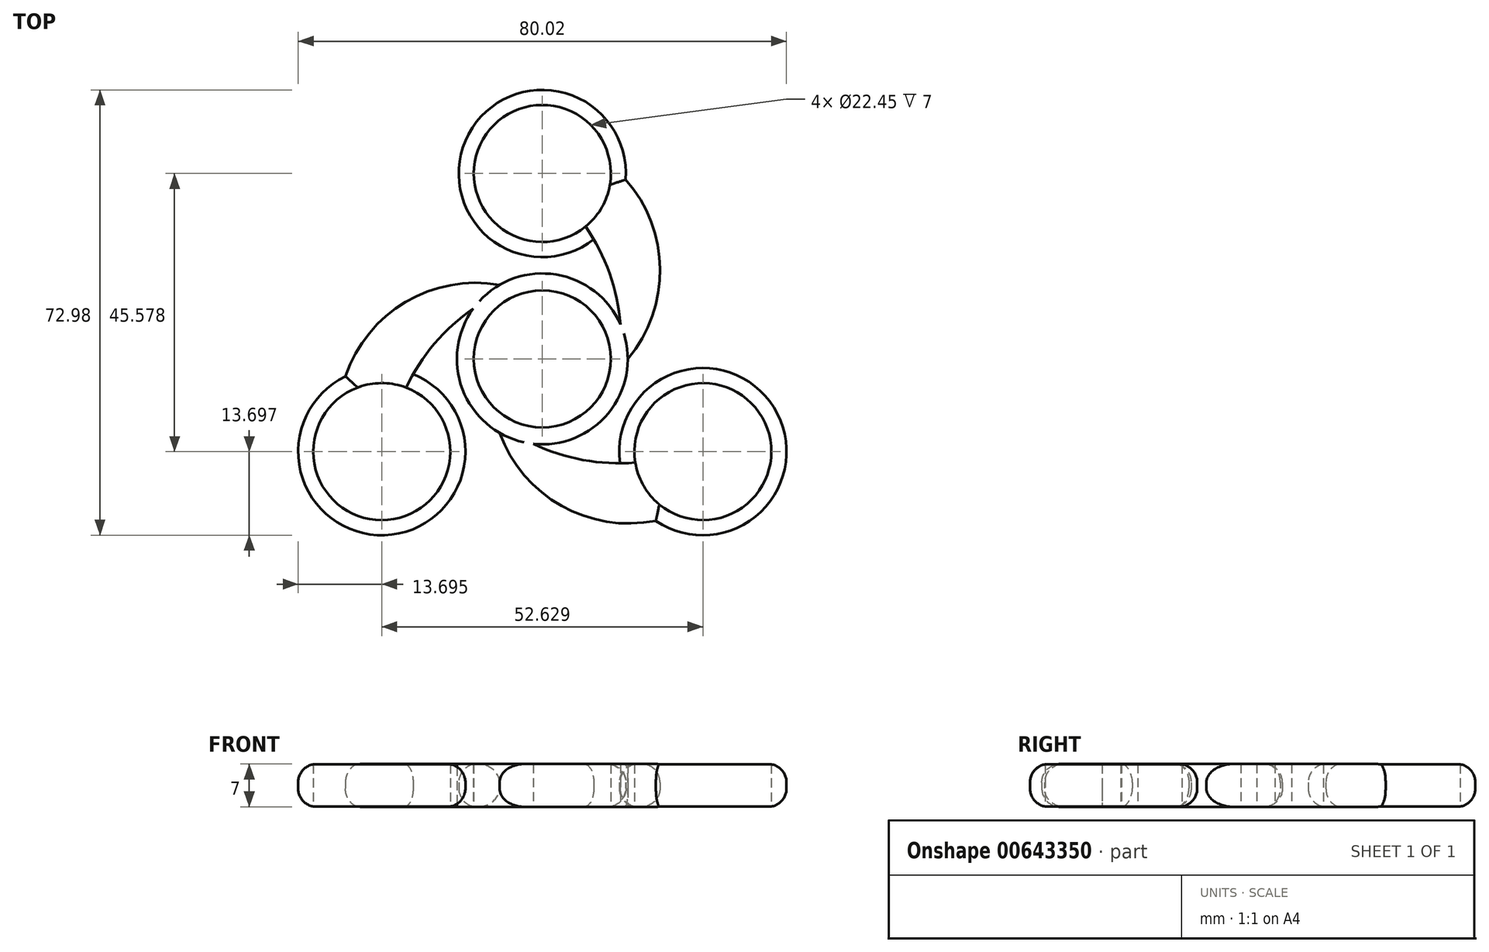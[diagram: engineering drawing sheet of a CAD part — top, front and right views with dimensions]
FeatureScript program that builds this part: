
annotation { "Feature Type Name" : "Feature", "Feature Type Description" : "" }
export const myFeature = defineFeature(function(context is Context, id is Id, definition is map)
    precondition{}
    {
        {
            var Q0;
            Q0=qCreatedBy(makeId("Top.planeOp"),FACE);
            var sketch = newSketch(context, id + "F0", { "sketchPlane" : qUnion([Q0])});
            skCircle(sketch, "E0", {"center": v(0, 0) * mm, "radius": 11.23 * mm});
            skArc(sketch, "E1", {"start": v(12.8, 5.66) * mm, "mid": v(4.34, 13.3) * mm, "end": v(-7, 12.12) * mm});
            skArc(sketch, "E2", {"start": v(13.66, 29.38) * mm, "mid": v(-12.09, 36.84) * mm, "end": v(8.43, 19.59) * mm});
            skCircle(sketch, "E3", {"center": v(0, 30.39) * mm, "radius": 11.23 * mm});
            skArc(sketch, "E4", {"start": v(12.8, 5.66) * mm, "mid": v(11.4, 12.87) * mm, "end": v(8.43, 19.59) * mm});
            skArc(sketch, "E5", {"start": v(14, 0) * mm, "mid": v(19.28, 14.75) * mm, "end": v(13.66, 29.38) * mm});
            skArc(sketch, "E6.1.0", {"start": v(-11.3, 8.26) * mm, "mid": v(-16.85, 3.44) * mm, "end": v(-21.18, -2.5) * mm});
            skArc(sketch, "E6.1.1", {"start": v(-7, 12.12) * mm, "mid": v(-22.42, 9.32) * mm, "end": v(-32.28, -2.86) * mm});
            skCircle(sketch, "E6.1.2", {"center": v(-26.31, -15.2) * mm, "radius": 11.23 * mm});
            skArc(sketch, "E6.1.3", {"start": v(-32.28, -2.86) * mm, "mid": v(-25.86, -28.89) * mm, "end": v(-21.18, -2.5) * mm});
            skArc(sketch, "E6.2.0", {"start": v(-1.5, -13.92) * mm, "mid": v(5.44, -16.31) * mm, "end": v(12.75, -17.1) * mm});
            skArc(sketch, "E6.2.1", {"start": v(-7, -12.12) * mm, "mid": v(3.14, -24.07) * mm, "end": v(18.62, -26.52) * mm});
            skCircle(sketch, "E6.2.2", {"center": v(26.31, -15.2) * mm, "radius": 11.23 * mm});
            skArc(sketch, "E6.2.3", {"start": v(18.62, -26.52) * mm, "mid": v(37.95, -7.95) * mm, "end": v(12.75, -17.1) * mm});
            skArc(sketch, "E7.trimOffspring", {"start": v(-1.5, -13.92) * mm, "mid": v(9.35, -10.42) * mm, "end": v(14, 0) * mm});
            skArc(sketch, "E8.trimOffspring", {"start": v(-11.3, 8.26) * mm, "mid": v(-13.7, -2.9) * mm, "end": v(-7, -12.12) * mm});
            skSolve(sketch);
        }
        {
            var Q0;
            Q0 = qSketchRegion(id + "F0", true);
            extrude(context, id + "F1", {"entities" : qUnion([Q0]), "depth" : 7 * mm, "offsetDistance" : 25 * mm});
        }
        {
            var Q0;
            Q0=makeQuery(id+"F1.opExtrude","CAP_EDGE",EDGE,{"disambiguationData":[OSD([sQuery(id+"F0.wireOp",EDGE,"E2")])],"isStart":false});
            var Q1;
            Q1=makeQuery(id+"F1.opExtrude","CAP_EDGE",EDGE,{"disambiguationData":[OSD([sQuery(id+"F0.wireOp",EDGE,"E6.2.3")])],"isStart":false});
            var Q2;
            Q2=makeQuery(id+"F1.opExtrude","CAP_EDGE",EDGE,{"disambiguationData":[OSD([sQuery(id+"F0.wireOp",EDGE,"E6.1.3")])],"isStart":false});
            fillet(context, id + "F2", {"entities" : qUnion([Q0, Q1, Q2]), "radius" : 3 * mm, "tangentPropagation" : true, "allowEdgeOverflow" : false});
        }
        {
            var Q0;
            Q0=makeQuery(id+"F1.opExtrude","CAP_EDGE",EDGE,{"disambiguationData":[OSD([sQuery(id+"F0.wireOp",EDGE,"E6.1.1")])],"isStart":false});
            var Q1;
            Q1=makeQuery(id+"F1.opExtrude","CAP_EDGE",EDGE,{"disambiguationData":[OSD([sQuery(id+"F0.wireOp",EDGE,"E5")])],"isStart":false});
            var Q2;
            Q2=makeQuery(id+"F1.opExtrude","CAP_EDGE",EDGE,{"disambiguationData":[OSD([sQuery(id+"F0.wireOp",EDGE,"E6.2.1")])],"isStart":false});
            fillet(context, id + "F3", {"entities" : qUnion([Q0, Q1, Q2]), "radius" : 3 * mm, "tangentPropagation" : true, "allowEdgeOverflow" : false});
        }
        {
            var Q0;
            Q0=makeQuery(id+"F1.opExtrude","CAP_EDGE",EDGE,{"disambiguationData":[OSD([sQuery(id+"F0.wireOp",EDGE,"E6.1.3")])],"isStart":true});
            var Q1;
            Q1=makeQuery(id+"F1.opExtrude","CAP_EDGE",EDGE,{"disambiguationData":[OSD([sQuery(id+"F0.wireOp",EDGE,"E6.1.1")])],"isStart":true});
            var Q2;
            Q2=makeQuery(id+"F1.opExtrude","CAP_EDGE",EDGE,{"disambiguationData":[OSD([sQuery(id+"F0.wireOp",EDGE,"E2")])],"isStart":true});
            var Q3;
            Q3=makeQuery(id+"F1.opExtrude","CAP_EDGE",EDGE,{"disambiguationData":[OSD([sQuery(id+"F0.wireOp",EDGE,"E5")])],"isStart":true});
            var Q4;
            Q4=makeQuery(id+"F1.opExtrude","CAP_EDGE",EDGE,{"disambiguationData":[OSD([sQuery(id+"F0.wireOp",EDGE,"E6.2.3")])],"isStart":true});
            var Q5;
            Q5=makeQuery(id+"F1.opExtrude","CAP_EDGE",EDGE,{"disambiguationData":[OSD([sQuery(id+"F0.wireOp",EDGE,"E6.2.1")])],"isStart":true});
            fillet(context, id + "F4", {"entities" : qUnion([Q0, Q1, Q2, Q3, Q4, Q5]), "radius" : 3 * mm, "tangentPropagation" : true, "allowEdgeOverflow" : false});
        }
    });
